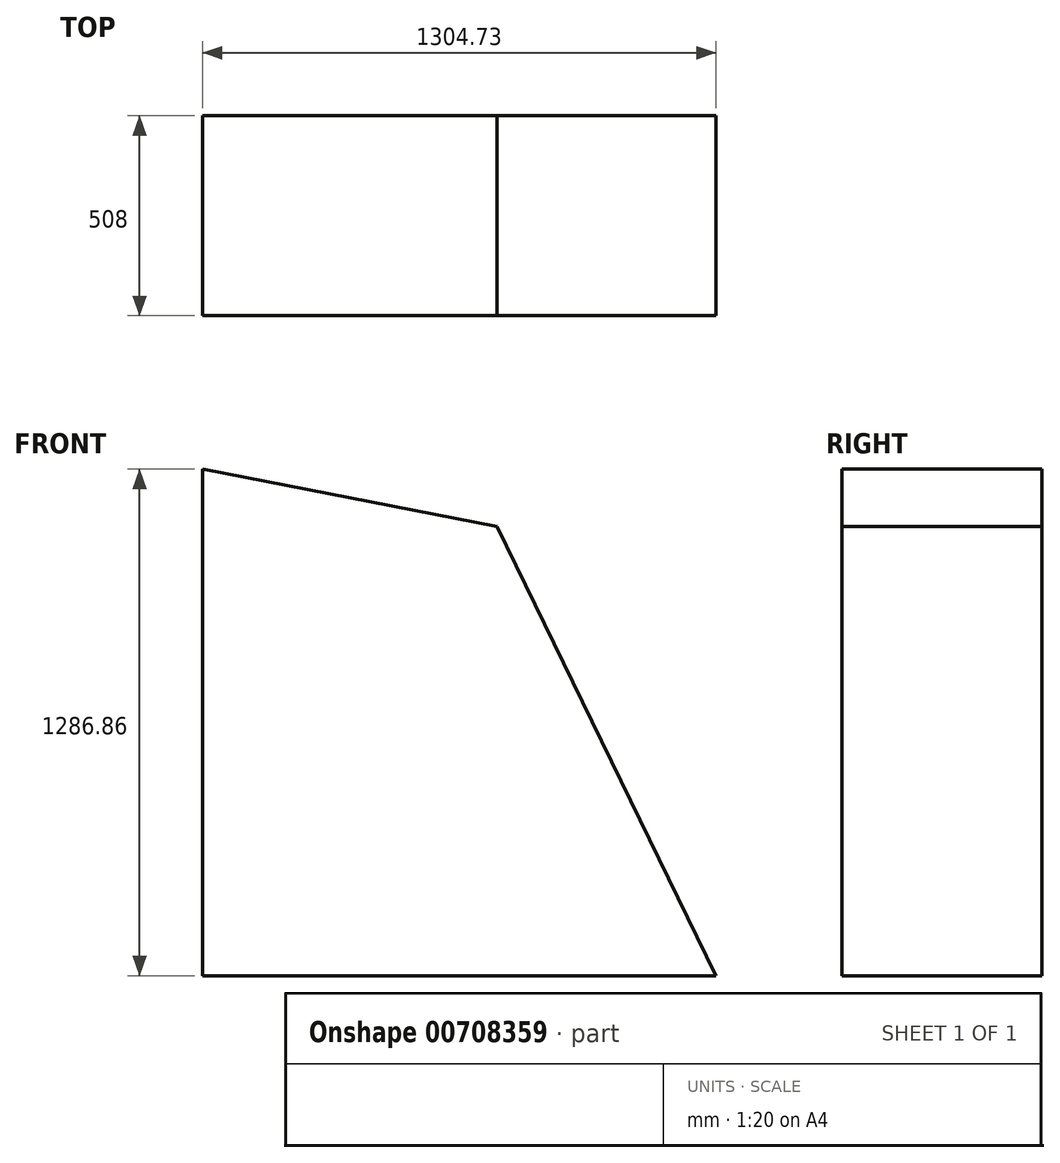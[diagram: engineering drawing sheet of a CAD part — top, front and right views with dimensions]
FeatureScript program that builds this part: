
annotation { "Feature Type Name" : "Feature", "Feature Type Description" : "" }
export const myFeature = defineFeature(function(context is Context, id is Id, definition is map)
    precondition{}
    {
        {
            var Q0;
            Q0=qCreatedBy(makeId("Front.planeOp"),FACE);
            var sketch = newSketch(context, id + "F0", { "sketchPlane" : qUnion([Q0])});
            skLineSegment(sketch, "E0", {"start": v(0, 0) * mm, "end": v(0, 0) * mm});
            skLineSegment(sketch, "E1", {"start": v(0, 0) * mm, "end": v(1304.73, 0) * mm});
            skLineSegment(sketch, "E2", {"start": v(1304.73, 0) * mm, "end": v(748, 1141.47) * mm});
            skLineSegment(sketch, "E3", {"start": v(748, 1141.47) * mm, "end": v(0, 1286.86) * mm});
            skLineSegment(sketch, "E4", {"start": v(0, 1286.86) * mm, "end": v(0, 0) * mm});
            skSolve(sketch);
        }
        {
            var Q0;
            Q0 = qSketchRegion(id + "F0", true);
            extrude(context, id + "F1", {"entities" : qUnion([Q0]), "depth" : 508 * mm, "offsetDistance" : 25.4 * mm});
        }
    });
